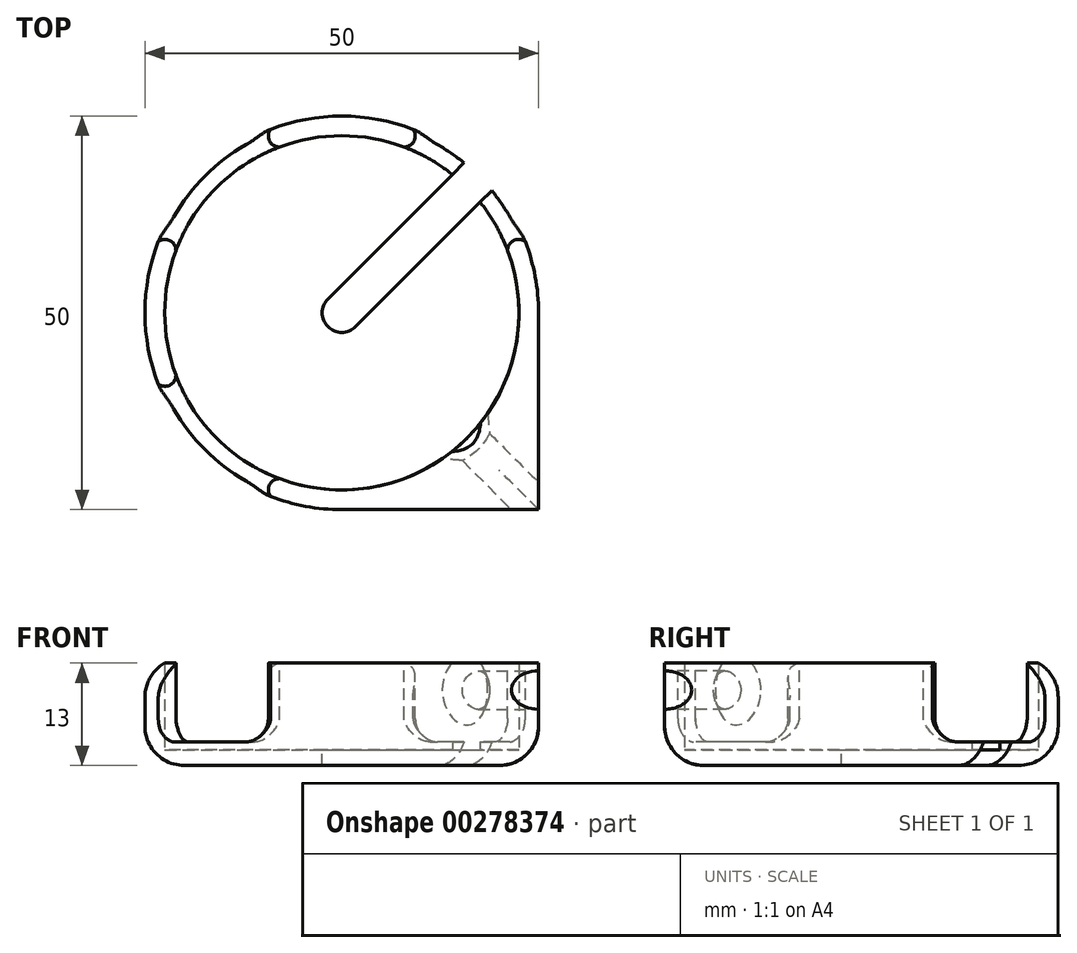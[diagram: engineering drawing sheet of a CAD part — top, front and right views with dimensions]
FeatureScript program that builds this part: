
annotation { "Feature Type Name" : "Feature", "Feature Type Description" : "" }
export const myFeature = defineFeature(function(context is Context, id is Id, definition is map)
    precondition{}
    {
        {
            var Q0;
            Q0=qCreatedBy(makeId("Top.planeOp"),FACE);
            var sketch = newSketch(context, id + "F0", { "sketchPlane" : qUnion([Q0])});
            skCircle(sketch, "E0", {"center": v(0, 0) * mm, "radius": 22.5 * mm});
            skCircle(sketch, "E1", {"center": v(0, 0) * mm, "radius": 25 * mm});
            skSolve(sketch);
        }
        {
            var Q0;
            Q0=makeQuery(id+"F0.imprint","IMPRINT",FACE,{"disambiguationData":[TD([[makeQuery(id+"F0.imprint","IMPRINT",EDGE,{"derivedFrom":sQuery(id+"F0.wireOp",EDGE,"E0")}),1.0]])]});
            extrude(context, id + "F1", {"entities" : qUnion([Q0]), "depth" : 2 * mm});
        }
        {
            var Q0;
            Q0 = qSketchRegion(id + "F0", true);
            extrude(context, id + "F2", {"entities" : qUnion([Q0]), "operationType" : NewBodyOperationType.ADD, "depth" : 13 * mm});
        }
        {
            var Q0;
            Q0=makeQuery(id+"F2.opExtrude","CAP_FACE",FACE,{"disambiguationData":[OSD([sQuery(id+"F0.wireOp",EDGE,"E0"),sQuery(id+"F0.wireOp",EDGE,"E1")])],"isStart":false});
            var sketch = newSketch(context, id + "F3", { "sketchPlane" : qUnion([Q0])});
            skLineSegment(sketch, "E2", {"start": v(25, 0) * mm, "end": v(25, -25) * mm});
            skLineSegment(sketch, "E3", {"start": v(0, -25) * mm, "end": v(25, -25) * mm});
            skArc(sketch, "E4", {"start": v(0, -25) * mm, "mid": v(17.68, -17.68) * mm, "end": v(25, 0) * mm});
            skSolve(sketch);
        }
        {
            var Q0;
            Q0 = qSketchRegion(id + "F3", true);
            var Q1;
            {var subQ0=sQuery(id+"F0.wireOp",EDGE,"E0");Q1=makeQuery(id+"F2.boolean.opBoolean","MERGE",FACE,{"derivedFrom":[makeQuery(id+"F1.opExtrude","CAP_FACE",FACE,{"disambiguationData":[OSD([subQ0])],"isStart":true}),makeQuery(id+"F2.opExtrude","CAP_FACE",FACE,{"disambiguationData":[OSD([subQ0,sQuery(id+"F0.wireOp",EDGE,"E1")])],"isStart":true})]});}
            extrude(context, id + "F4", {"entities" : qUnion([Q0]), "operationType" : NewBodyOperationType.ADD, "endBound" : BoundingType.UP_TO_SURFACE, "oppositeDirection" : true, "endBoundEntityFace" : qUnion([Q1]), "depth" : 25 * mm});
        }
        {
            var Q0;
            Q0=qCreatedBy(makeId("Top.planeOp"),FACE);
            var sketch = newSketch(context, id + "F5", { "sketchPlane" : qUnion([Q0])});
            skLineSegment(sketch, "E5", {"start": v(57.61, -10.18) * mm, "end": v(11.2, -56.58) * mm, "construction": true});
            skSolve(sketch);
        }
        {
            var Q0;
            Q0=sQuery(id+"F5.wireOp",EDGE,"E5");
            cPlane(context, id + "F6", {"entities" : qUnion([Q0]), "cplaneType" : CPlaneType.LINE_ANGLE, "offset" : 25 * mm, "angle" : 90 * degree, "width" : 150 * mm, "height" : 150 * mm});
        }
        {
            var Q0;
            Q0=qCreatedBy(id+"F6.planeOp",FACE);
            var sketch = newSketch(context, id + "F7", { "sketchPlane" : qUnion([Q0])});
            skCircle(sketch, "E6", {"center": v(0, 9.58) * mm, "radius": 2.44 * mm});
            skSolve(sketch);
        }
        {
            var Q0;
            Q0 = qSketchRegion(id + "F7", true);
            extrude(context, id + "F8", {"entities" : qUnion([Q0]), "operationType" : NewBodyOperationType.REMOVE, "oppositeDirection" : true, "depth" : 35.2 * mm});
        }
        {
            var Q0;
            Q0=makeQuery(id+"F4.boolean.opBoolean","MERGE",FACE,{"derivedFrom":[makeQuery(id+"F2.opExtrude","CAP_FACE",FACE,{"disambiguationData":[OSD([sQuery(id+"F0.wireOp",EDGE,"E0"),sQuery(id+"F0.wireOp",EDGE,"E1")])],"isStart":false}),makeQuery(id+"F4.opExtrude","CAP_FACE",FACE,{"disambiguationData":[OSD([sQuery(id+"F3.wireOp",EDGE,"E2"),sQuery(id+"F3.wireOp",EDGE,"E3"),sQuery(id+"F3.wireOp",EDGE,"E4")])],"isStart":true})]});
            var sketch = newSketch(context, id + "F9", { "sketchPlane" : qUnion([Q0])});
            skLineSegment(sketch, "E7", {"start": v(27.84, 27.84) * mm, "end": v(-33.73, -33.73) * mm, "construction": true});
            skLineSegment(sketch, "E8", {"start": v(8.48, -8.48) * mm, "end": v(-38.85, 38.85) * mm, "construction": true});
            skArc(sketch, "E9", {"start": v(-9.04, 23.3) * mm, "mid": v(-9.18, 21.82) * mm, "end": v(-7.89, 21.07) * mm});
            skArc(sketch, "E10.MirrorCS", {"start": v(-23.3, 9.04) * mm, "mid": v(-21.82, 9.18) * mm, "end": v(-21.07, 7.89) * mm});
            skArc(sketch, "E11", {"start": v(-7.89, 21.07) * mm, "mid": v(-15.65, 15.65) * mm, "end": v(-21.07, 7.89) * mm});
            skArc(sketch, "E12", {"start": v(-9.04, 23.3) * mm, "mid": v(-17.9, 17.9) * mm, "end": v(-23.3, 9.04) * mm});
            skArc(sketch, "E13.MirrorCS", {"start": v(23.3, 9.04) * mm, "mid": v(21.82, 9.18) * mm, "end": v(21.07, 7.89) * mm});
            skArc(sketch, "E14.MirrorCS", {"start": v(9.04, 23.3) * mm, "mid": v(17.9, 17.9) * mm, "end": v(23.3, 9.04) * mm});
            skArc(sketch, "E15.MirrorCS", {"start": v(7.89, 21.07) * mm, "mid": v(15.65, 15.65) * mm, "end": v(21.07, 7.89) * mm});
            skLineSegment(sketch, "E16.MirrorCS", {"start": v(-8.48, -8.48) * mm, "end": v(38.85, 38.85) * mm, "construction": true});
            skArc(sketch, "E17.MirrorCS", {"start": v(9.04, 23.3) * mm, "mid": v(9.18, 21.82) * mm, "end": v(7.89, 21.07) * mm});
            skArc(sketch, "E18.MirrorCS", {"start": v(-9.04, -23.3) * mm, "mid": v(-9.18, -21.82) * mm, "end": v(-7.89, -21.07) * mm});
            skLineSegment(sketch, "E19.MirrorCS", {"start": v(8.48, 8.48) * mm, "end": v(-38.85, -38.85) * mm, "construction": true});
            skArc(sketch, "E20.MirrorCS", {"start": v(-23.3, -9.04) * mm, "mid": v(-21.82, -9.18) * mm, "end": v(-21.07, -7.89) * mm});
            skArc(sketch, "E21.MirrorCS", {"start": v(-7.89, -21.07) * mm, "mid": v(-15.65, -15.65) * mm, "end": v(-21.07, -7.89) * mm});
            skArc(sketch, "E22.MirrorCS", {"start": v(-9.04, -23.3) * mm, "mid": v(-17.9, -17.9) * mm, "end": v(-23.3, -9.04) * mm});
            skSolve(sketch);
        }
        {
            var Q0;
            Q0 = qSketchRegion(id + "F9", true);
            extrude(context, id + "F10", {"entities" : qUnion([Q0]), "operationType" : NewBodyOperationType.REMOVE, "oppositeDirection" : true, "depth" : 10 * mm});
        }
        {
            var Q0;
            {var subQ0=sQuery(id+"F0.wireOp",EDGE,"E1");Q0=makeQuery(id+"F10.boolean.opBoolean","SPLIT",EDGE,{"disambiguationData":[TD([makeQuery(id+"F10.opExtrude","SWEPT_FACE",FACE,{"disambiguationData":[OSD([sQuery(id+"F9.wireOp",EDGE,"E9")])]})])],"derivedFrom":makeQuery(id+"F2.opExtrude","CAP_EDGE",EDGE,{"disambiguationData":[OSD([subQ0])],"isStart":false})});}
            var Q1;
            {var subQ0=sQuery(id+"F0.wireOp",EDGE,"E1");Q1=makeQuery(id+"F10.boolean.opBoolean","SPLIT",EDGE,{"disambiguationData":[TD([makeQuery(id+"F10.opExtrude","SWEPT_FACE",FACE,{"disambiguationData":[OSD([sQuery(id+"F9.wireOp",EDGE,"E10.MirrorCS")])]})])],"derivedFrom":makeQuery(id+"F2.opExtrude","CAP_EDGE",EDGE,{"disambiguationData":[OSD([subQ0])],"isStart":false})});}
            var Q2;
            Q2=makeQuery(id+"F2.opExtrude","CAP_EDGE",EDGE,{"disambiguationData":[OSD([sQuery(id+"F0.wireOp",EDGE,"E1")])],"isStart":true});
            fillet(context, id + "F11", {"entities" : qUnion([Q0, Q1, Q2]), "radius" : 5 * mm, "tangentPropagation" : true, "allowEdgeOverflow" : false});
        }
        {
            var Q0;
            Q0=makeQuery(id+"F10.boolean.opBoolean","COPY",EDGE,{"derivedFrom":makeQuery(id+"F10.opExtrude","CAP_EDGE",EDGE,{"disambiguationData":[OSD([sQuery(id+"F9.wireOp",EDGE,"E18.MirrorCS")])],"isStart":false})});
            var Q1;
            Q1=makeQuery(id+"F10.boolean.opBoolean","COPY",EDGE,{"derivedFrom":makeQuery(id+"F10.opExtrude","CAP_EDGE",EDGE,{"disambiguationData":[OSD([sQuery(id+"F9.wireOp",EDGE,"E20.MirrorCS")])],"isStart":false})});
            var Q2;
            Q2=makeQuery(id+"F10.boolean.opBoolean","COPY",EDGE,{"derivedFrom":makeQuery(id+"F10.opExtrude","CAP_EDGE",EDGE,{"disambiguationData":[OSD([sQuery(id+"F9.wireOp",EDGE,"E10.MirrorCS")])],"isStart":false})});
            var Q3;
            Q3=makeQuery(id+"F10.boolean.opBoolean","COPY",EDGE,{"derivedFrom":makeQuery(id+"F10.opExtrude","CAP_EDGE",EDGE,{"disambiguationData":[OSD([sQuery(id+"F9.wireOp",EDGE,"E9")])],"isStart":false})});
            var Q4;
            Q4=makeQuery(id+"F10.boolean.opBoolean","COPY",EDGE,{"derivedFrom":makeQuery(id+"F10.opExtrude","CAP_EDGE",EDGE,{"disambiguationData":[OSD([sQuery(id+"F9.wireOp",EDGE,"E17.MirrorCS")])],"isStart":false})});
            var Q5;
            Q5=makeQuery(id+"F10.boolean.opBoolean","COPY",EDGE,{"derivedFrom":makeQuery(id+"F10.opExtrude","CAP_EDGE",EDGE,{"disambiguationData":[OSD([sQuery(id+"F9.wireOp",EDGE,"E13.MirrorCS")])],"isStart":false})});
            fillet(context, id + "F12", {"entities" : qUnion([Q0, Q1, Q2, Q3, Q4, Q5]), "radius" : 3 * mm, "tangentPropagation" : true, "allowEdgeOverflow" : false});
        }
        {
            var Q0;
            Q0=makeQuery(id+"F1.opExtrude","CAP_FACE",FACE,{"disambiguationData":[OSD([sQuery(id+"F0.wireOp",EDGE,"E0")])],"isStart":false});
            var sketch = newSketch(context, id + "F13", { "sketchPlane" : qUnion([Q0])});
            skArc(sketch, "E23", {"start": v(-1.77, 1.77) * mm, "mid": v(-1.77, -1.77) * mm, "end": v(1.77, -1.77) * mm});
            skLineSegment(sketch, "E24", {"start": v(-1.77, 1.77) * mm, "end": v(18.64, 22.17) * mm});
            skLineSegment(sketch, "E25", {"start": v(1.77, -1.77) * mm, "end": v(22.17, 18.64) * mm});
            skLineSegment(sketch, "E26", {"start": v(18.64, 22.17) * mm, "end": v(22.17, 18.64) * mm});
            skSolve(sketch);
        }
        {
            var Q0;
            Q0 = qSketchRegion(id + "F13", true);
            extrude(context, id + "F14", {"entities" : qUnion([Q0]), "operationType" : NewBodyOperationType.REMOVE, "oppositeDirection" : true, "depth" : 25 * mm, "hasSecondDirection" : true, "secondDirectionOppositeDirection" : false, "secondDirectionDepth" : 25 * mm});
        }
        {
            var Q0;
            Q0=makeQuery(id+"F8.boolean.opBoolean","INTERSECT",EDGE,{"derivedFrom":[makeQuery(id+"F2.opExtrude","SWEPT_FACE",FACE,{"disambiguationData":[OSD([sQuery(id+"F0.wireOp",EDGE,"E0")])]}),makeQuery(id+"F8.opExtrude","SWEPT_FACE",FACE,{"disambiguationData":[OSD([sQuery(id+"F7.wireOp",EDGE,"E6")])]})]});
            chamfer(context, id + "F15", {"entities" : qUnion([Q0]), "width" : 2 * mm, "tangentPropagation" : true});
        }
    });
